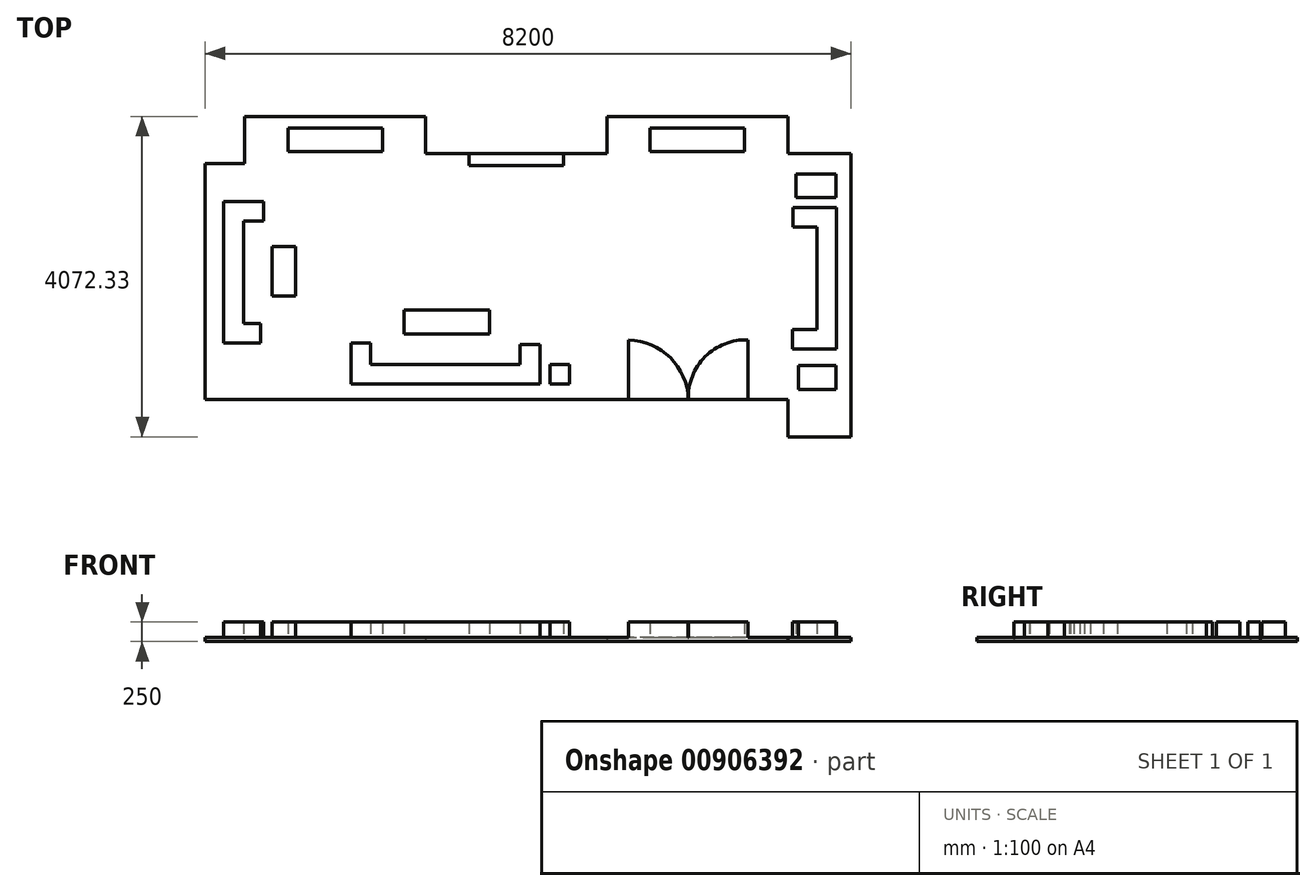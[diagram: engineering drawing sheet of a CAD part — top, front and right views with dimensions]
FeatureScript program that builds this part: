
annotation { "Feature Type Name" : "Feature", "Feature Type Description" : "" }
export const myFeature = defineFeature(function(context is Context, id is Id, definition is map)
    precondition{}
    {
        {
            var Q0;
            Q0=qCreatedBy(makeId("Top.planeOp"),FACE);
            var sketch = newSketch(context, id + "F0", { "sketchPlane" : qUnion([Q0])});
            skLineSegment(sketch, "E0", {"start": v(-4707.84, -1486.14) * mm, "end": v(-4707.84, 1513.86) * mm});
            skLineSegment(sketch, "E1", {"start": v(-4707.84, 1513.86) * mm, "end": v(-4207.84, 1513.86) * mm});
            skLineSegment(sketch, "E2", {"start": v(-4207.84, 1513.86) * mm, "end": v(-4207.84, 2113.86) * mm});
            skLineSegment(sketch, "E3", {"start": v(-4207.84, 2113.86) * mm, "end": v(-1907.84, 2113.86) * mm});
            skLineSegment(sketch, "E4", {"start": v(-1907.84, 2113.86) * mm, "end": v(-1907.84, 1641.53) * mm});
            skLineSegment(sketch, "E5", {"start": v(-1907.84, 1641.53) * mm, "end": v(392.16, 1641.53) * mm});
            skLineSegment(sketch, "E6", {"start": v(392.16, 1641.53) * mm, "end": v(392.16, 2113.86) * mm});
            skLineSegment(sketch, "E7", {"start": v(392.16, 2113.86) * mm, "end": v(2692.16, 2113.86) * mm});
            skLineSegment(sketch, "E8", {"start": v(2692.16, 2113.86) * mm, "end": v(2692.16, 1641.53) * mm});
            skLineSegment(sketch, "E9", {"start": v(2692.16, 1641.53) * mm, "end": v(3492.16, 1641.53) * mm});
            skLineSegment(sketch, "E10", {"start": v(3492.16, 1641.53) * mm, "end": v(3492.16, -1958.47) * mm});
            skLineSegment(sketch, "E11", {"start": v(3492.16, -1958.47) * mm, "end": v(2692.16, -1958.47) * mm});
            skLineSegment(sketch, "E12", {"start": v(2692.16, -1958.47) * mm, "end": v(2692.16, -1486.14) * mm});
            skLineSegment(sketch, "E13", {"start": v(2692.16, -1486.14) * mm, "end": v(-4707.84, -1486.14) * mm});
            skSolve(sketch);
        }
        {
            var Q0;
            Q0 = qSketchRegion(id + "F0", true);
            extrude(context, id + "F1", {"entities" : qUnion([Q0]), "depth" : 50 * mm, "offsetDistance" : 25 * mm});
        }
        {
            var Q0;
            Q0=makeQuery(id+"F1.opExtrude","CAP_FACE",FACE,{"disambiguationData":[OSD([sQuery(id+"F0.wireOp",EDGE,"E0"),sQuery(id+"F0.wireOp",EDGE,"E1"),sQuery(id+"F0.wireOp",EDGE,"E2"),sQuery(id+"F0.wireOp",EDGE,"E3"),sQuery(id+"F0.wireOp",EDGE,"E4"),sQuery(id+"F0.wireOp",EDGE,"E5"),sQuery(id+"F0.wireOp",EDGE,"E6"),sQuery(id+"F0.wireOp",EDGE,"E7"),sQuery(id+"F0.wireOp",EDGE,"E8"),sQuery(id+"F0.wireOp",EDGE,"E9"),sQuery(id+"F0.wireOp",EDGE,"E10"),sQuery(id+"F0.wireOp",EDGE,"E11"),sQuery(id+"F0.wireOp",EDGE,"E12"),sQuery(id+"F0.wireOp",EDGE,"E13")])],"isStart":false});
            var sketch = newSketch(context, id + "F2", { "sketchPlane" : qUnion([Q0])});
            skLineSegment(sketch, "E14", {"start": v(-3657.84, 1963.86) * mm, "end": v(-3657.84, 1663.86) * mm});
            skLineSegment(sketch, "E15", {"start": v(-3657.84, 1663.86) * mm, "end": v(-2457.84, 1663.86) * mm});
            skLineSegment(sketch, "E16", {"start": v(-3967.6, 1032.18) * mm, "end": v(-4473.37, 1032.18) * mm});
            skLineSegment(sketch, "E17", {"start": v(-4473.37, 1032.18) * mm, "end": v(-4473.37, -767.82) * mm});
            skLineSegment(sketch, "E18", {"start": v(-4473.37, -767.82) * mm, "end": v(-4002.17, -767.82) * mm});
            skLineSegment(sketch, "E19", {"start": v(-4002.17, -767.82) * mm, "end": v(-4002.17, -517.82) * mm});
            skLineSegment(sketch, "E20", {"start": v(-4002.17, -517.82) * mm, "end": v(-4223.37, -517.82) * mm});
            skLineSegment(sketch, "E21", {"start": v(-4223.37, -517.82) * mm, "end": v(-4223.37, 782.18) * mm});
            skLineSegment(sketch, "E22", {"start": v(-4223.37, 782.18) * mm, "end": v(-3967.6, 782.18) * mm});
            skLineSegment(sketch, "E23", {"start": v(-3967.6, 782.18) * mm, "end": v(-3967.6, 1032.18) * mm});
            skLineSegment(sketch, "E24.bottom", {"start": v(-3860.96, 459.57) * mm, "end": v(-3560.96, 459.57) * mm});
            skLineSegment(sketch, "E24.top", {"start": v(-3860.96, -169.6) * mm, "end": v(-3560.96, -169.6) * mm});
            skLineSegment(sketch, "E24.left", {"start": v(-3860.96, 459.57) * mm, "end": v(-3860.96, -169.6) * mm});
            skLineSegment(sketch, "E24.right", {"start": v(-3560.96, 459.57) * mm, "end": v(-3560.96, -169.6) * mm});
            skLineSegment(sketch, "E25", {"start": v(-2857.13, -767.82) * mm, "end": v(-2857.13, -1289.33) * mm});
            skPoint(sketch, "E25.startSnap0", {"position": v(-4237.77, -767.82) * mm});
            skLineSegment(sketch, "E26", {"start": v(-2857.13, -1289.33) * mm, "end": v(-457.13, -1289.33) * mm});
            skLineSegment(sketch, "E27", {"start": v(-457.13, -1289.33) * mm, "end": v(-457.13, -783.4) * mm});
            skLineSegment(sketch, "E28", {"start": v(-457.13, -783.4) * mm, "end": v(-707.13, -783.4) * mm});
            skLineSegment(sketch, "E29", {"start": v(-707.13, -783.4) * mm, "end": v(-707.13, -1039.33) * mm});
            skLineSegment(sketch, "E30", {"start": v(-707.13, -1039.33) * mm, "end": v(-2607.13, -1039.33) * mm});
            skLineSegment(sketch, "E31", {"start": v(-2607.13, -1039.33) * mm, "end": v(-2607.13, -766.8) * mm});
            skLineSegment(sketch, "E32", {"start": v(-2607.13, -766.8) * mm, "end": v(-2857.13, -767.82) * mm});
            skLineSegment(sketch, "E33.bottom", {"start": v(-2185.3, -349.49) * mm, "end": v(-1097.57, -349.49) * mm});
            skLineSegment(sketch, "E33.top", {"start": v(-2185.3, -649.49) * mm, "end": v(-1097.57, -649.49) * mm});
            skLineSegment(sketch, "E33.left", {"start": v(-2185.3, -349.49) * mm, "end": v(-2185.3, -649.49) * mm});
            skLineSegment(sketch, "E33.right", {"start": v(-1097.57, -349.49) * mm, "end": v(-1097.57, -649.49) * mm});
            skPoint(sketch, "E34.firstSnap0", {"position": v(-457.13, -1036.36) * mm});
            skLineSegment(sketch, "E34.bottom", {"start": v(-329.77, -1036.36) * mm, "end": v(-79.77, -1036.36) * mm});
            skLineSegment(sketch, "E34.top", {"start": v(-329.77, -1286.36) * mm, "end": v(-79.77, -1286.36) * mm});
            skLineSegment(sketch, "E34.left", {"start": v(-329.77, -1036.36) * mm, "end": v(-329.77, -1286.36) * mm});
            skLineSegment(sketch, "E34.right", {"start": v(-79.77, -1036.36) * mm, "end": v(-79.77, -1286.36) * mm});
            skLineSegment(sketch, "E35.bottom", {"start": v(-1355.64, 1641.53) * mm, "end": v(-155.64, 1641.53) * mm});
            skLineSegment(sketch, "E35.top", {"start": v(-1355.64, 1488.53) * mm, "end": v(-155.64, 1488.53) * mm});
            skLineSegment(sketch, "E35.left", {"start": v(-1355.64, 1641.53) * mm, "end": v(-1355.64, 1488.53) * mm});
            skLineSegment(sketch, "E35.right", {"start": v(-155.64, 1641.53) * mm, "end": v(-155.64, 1488.53) * mm});
            skLineSegment(sketch, "E36", {"start": v(942.16, 1663.86) * mm, "end": v(2142.16, 1663.86) * mm});
            skLineSegment(sketch, "E37", {"start": v(2142.16, 1663.86) * mm, "end": v(2142.16, 1963.86) * mm});
            skLineSegment(sketch, "E38.bottom", {"start": v(2796.46, 1383.16) * mm, "end": v(3301.39, 1383.16) * mm});
            skLineSegment(sketch, "E38.top", {"start": v(2796.46, 1083.16) * mm, "end": v(3301.39, 1083.16) * mm});
            skLineSegment(sketch, "E38.left", {"start": v(2796.46, 1383.16) * mm, "end": v(2796.46, 1083.16) * mm});
            skLineSegment(sketch, "E38.right", {"start": v(3301.39, 1383.16) * mm, "end": v(3301.39, 1083.16) * mm});
            skLineSegment(sketch, "E39", {"start": v(2758.58, 956.28) * mm, "end": v(3311.54, 956.28) * mm});
            skLineSegment(sketch, "E40", {"start": v(3311.54, 956.28) * mm, "end": v(3311.54, -843.72) * mm});
            skLineSegment(sketch, "E41", {"start": v(3311.54, -843.72) * mm, "end": v(2748.48, -843.72) * mm});
            skLineSegment(sketch, "E42", {"start": v(2748.48, -843.72) * mm, "end": v(2748.48, -593.72) * mm});
            skLineSegment(sketch, "E43", {"start": v(2748.48, -593.72) * mm, "end": v(3061.54, -593.72) * mm});
            skLineSegment(sketch, "E44", {"start": v(3061.54, -593.72) * mm, "end": v(3061.54, 706.28) * mm});
            skLineSegment(sketch, "E45", {"start": v(3061.54, 706.28) * mm, "end": v(2758.58, 706.28) * mm});
            skLineSegment(sketch, "E46", {"start": v(2758.58, 706.28) * mm, "end": v(2758.58, 956.28) * mm});
            skLineSegment(sketch, "E47.bottom", {"start": v(2826.76, -1054.29) * mm, "end": v(3301.39, -1054.29) * mm});
            skLineSegment(sketch, "E47.top", {"start": v(2826.76, -1354.29) * mm, "end": v(3301.39, -1354.29) * mm});
            skLineSegment(sketch, "E47.left", {"start": v(2826.76, -1054.29) * mm, "end": v(2826.76, -1354.29) * mm});
            skLineSegment(sketch, "E47.right", {"start": v(3301.39, -1054.29) * mm, "end": v(3301.39, -1354.29) * mm});
            skLineSegment(sketch, "E48", {"start": v(666.35, -1486.14) * mm, "end": v(1426.35, -1486.14) * mm});
            skLineSegment(sketch, "E49", {"start": v(666.35, -1486.14) * mm, "end": v(666.35, -726.14) * mm});
            skLineSegment(sketch, "E50", {"start": v(2188.35, -1486.14) * mm, "end": v(2188.35, -726.14) * mm});
            skArc(sketch, "E51", {"start": v(1426.35, -1486.14) * mm, "mid": v(1200.22, -952.27) * mm, "end": v(666.35, -726.14) * mm});
            skLineSegment(sketch, "E52", {"start": v(2188.35, -1486.14) * mm, "end": v(1428.35, -1486.14) * mm});
            skArc(sketch, "E53", {"start": v(2188.35, -726.14) * mm, "mid": v(1642.47, -940.26) * mm, "end": v(1428.35, -1486.14) * mm});
            skLineSegment(sketch, "E54", {"start": v(-3657.84, 1963.86) * mm, "end": v(-2457.84, 1963.86) * mm});
            skLineSegment(sketch, "E55", {"start": v(-2457.84, 1963.86) * mm, "end": v(-2457.84, 1663.86) * mm});
            skLineSegment(sketch, "E56", {"start": v(-4207.84, 2113.86) * mm, "end": v(-4207.84, 1513.86) * mm});
            skLineSegment(sketch, "E57", {"start": v(-1907.84, 2113.86) * mm, "end": v(-1907.84, 1641.53) * mm});
            skLineSegment(sketch, "E58", {"start": v(2142.16, 1963.86) * mm, "end": v(942.16, 1963.86) * mm});
            skLineSegment(sketch, "E59", {"start": v(942.16, 1963.86) * mm, "end": v(942.16, 1663.86) * mm});
            skLineSegment(sketch, "E60", {"start": v(2692.16, 2113.86) * mm, "end": v(2692.16, 1641.53) * mm});
            skSolve(sketch);
        }
        {
            var Q0;
            Q0=makeQuery(id+"F2.imprint","IMPRINT",FACE,{"disambiguationData":[TD([[makeQuery(id+"F2.imprint","IMPRINT",EDGE,{"derivedFrom":sQuery(id+"F2.wireOp",EDGE,"E14")}),1.0]])]});
            var Q1;
            Q1=makeQuery(id+"F2.imprint","IMPRINT",FACE,{"disambiguationData":[TD([[makeQuery(id+"F2.imprint","IMPRINT",EDGE,{"derivedFrom":sQuery(id+"F2.wireOp",EDGE,"E16")}),1.0]])]});
            var Q2;
            Q2=makeQuery(id+"F2.imprint","IMPRINT",FACE,{"disambiguationData":[TD([[makeQuery(id+"F2.imprint","IMPRINT",EDGE,{"derivedFrom":sQuery(id+"F2.wireOp",EDGE,"E24.bottom")}),-1.0]])]});
            var Q3;
            Q3=makeQuery(id+"F2.imprint","IMPRINT",FACE,{"disambiguationData":[TD([[makeQuery(id+"F2.imprint","IMPRINT",EDGE,{"derivedFrom":sQuery(id+"F2.wireOp",EDGE,"E25")}),1.0]])]});
            var Q4;
            Q4=makeQuery(id+"F2.imprint","IMPRINT",FACE,{"disambiguationData":[TD([[makeQuery(id+"F2.imprint","IMPRINT",EDGE,{"derivedFrom":sQuery(id+"F2.wireOp",EDGE,"E33.bottom")}),-1.0]])]});
            var Q5;
            Q5=makeQuery(id+"F2.imprint","IMPRINT",FACE,{"disambiguationData":[TD([[makeQuery(id+"F2.imprint","IMPRINT",EDGE,{"derivedFrom":sQuery(id+"F2.wireOp",EDGE,"E34.bottom")}),-1.0]])]});
            var Q6;
            Q6=makeQuery(id+"F2.imprint","IMPRINT",FACE,{"disambiguationData":[TD([[makeQuery(id+"F2.imprint","IMPRINT",EDGE,{"derivedFrom":sQuery(id+"F2.wireOp",EDGE,"E35.bottom")}),-1.0]])]});
            var Q7;
            Q7=makeQuery(id+"F2.imprint","IMPRINT",FACE,{"disambiguationData":[TD([[makeQuery(id+"F2.imprint","IMPRINT",EDGE,{"derivedFrom":sQuery(id+"F2.wireOp",EDGE,"l3PRhV3f-7AM1-lNvs-EItF-MUQrPMaBAiv7")}),1.0]])]});
            var Q8;
            Q8=makeQuery(id+"F2.imprint","IMPRINT",FACE,{"disambiguationData":[TD([[makeQuery(id+"F2.imprint","IMPRINT",EDGE,{"derivedFrom":sQuery(id+"F2.wireOp",EDGE,"E38.bottom")}),-1.0]])]});
            var Q9;
            Q9=makeQuery(id+"F2.imprint","IMPRINT",FACE,{"disambiguationData":[TD([[makeQuery(id+"F2.imprint","IMPRINT",EDGE,{"derivedFrom":sQuery(id+"F2.wireOp",EDGE,"E39")}),-1.0]])]});
            var Q10;
            Q10=makeQuery(id+"F2.imprint","IMPRINT",FACE,{"disambiguationData":[TD([[makeQuery(id+"F2.imprint","IMPRINT",EDGE,{"derivedFrom":sQuery(id+"F2.wireOp",EDGE,"E47.bottom")}),-1.0]])]});
            extrude(context, id + "F3", {"entities" : qUnion([Q0, Q1, Q2, Q3, Q4, Q5, Q6, Q7, Q8, Q9, Q10]), "operationType" : NewBodyOperationType.ADD, "depth" : 200 * mm, "offsetDistance" : 25 * mm});
        }
        {
            var Q0;
            Q0 = qSketchRegion(id + "F2", true);
            extrude(context, id + "F4", {"entities" : qUnion([Q0]), "operationType" : NewBodyOperationType.ADD, "depth" : 200 * mm, "offsetDistance" : 25 * mm});
        }
    });
